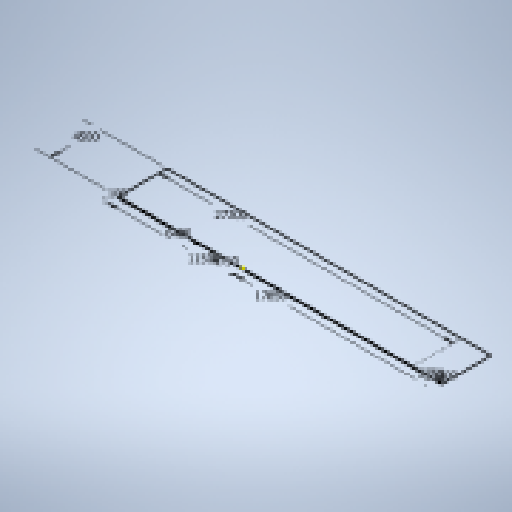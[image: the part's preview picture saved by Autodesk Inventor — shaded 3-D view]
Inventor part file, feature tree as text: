
AUTODESK INVENTOR PART (.ipt)
format: ipt  version: 2025 (Build 290162010, 162A)  size: 194,560 bytes
history: native  units: mm
features: extrude x3, sketch x2, other x2
ambient origin geometry x8: Origin, YZ Plane, XZ Plane, XY Plane, X Axis, Y Axis, Z Axis, Center Point
bodies: Solid1 (feature_tree)
feature tree (7):
  sketch  "Sketch1"  dims[d0=4500.0mm d1=27200.0mm]
  extrude  "Extrusion1"  Depth=4500.0mm
  extrude  "Extrusion2"  Depth=500.0mm
  extrude  "Extrusion3"  Depth=11500.0mm
  other  "Pillars"
  sketch  "Sketch Rectangular Pattern1"  dims[d2=300.0mm d3=500.0mm d4=11500.0mm d5=17850.0mm d6=2770.0mm d7=100.0mm d8=4750.0mm d9=6400.0mm d10=10.0mm d11=0.0mm d12=4000.0mm d13=0.0mm d14=50.0mm d16=6000.0mm d17=10.0mm d19=10.0mm d21=5350.0mm d22=300.0mm d23=0.0mm]
  other  "wall"
